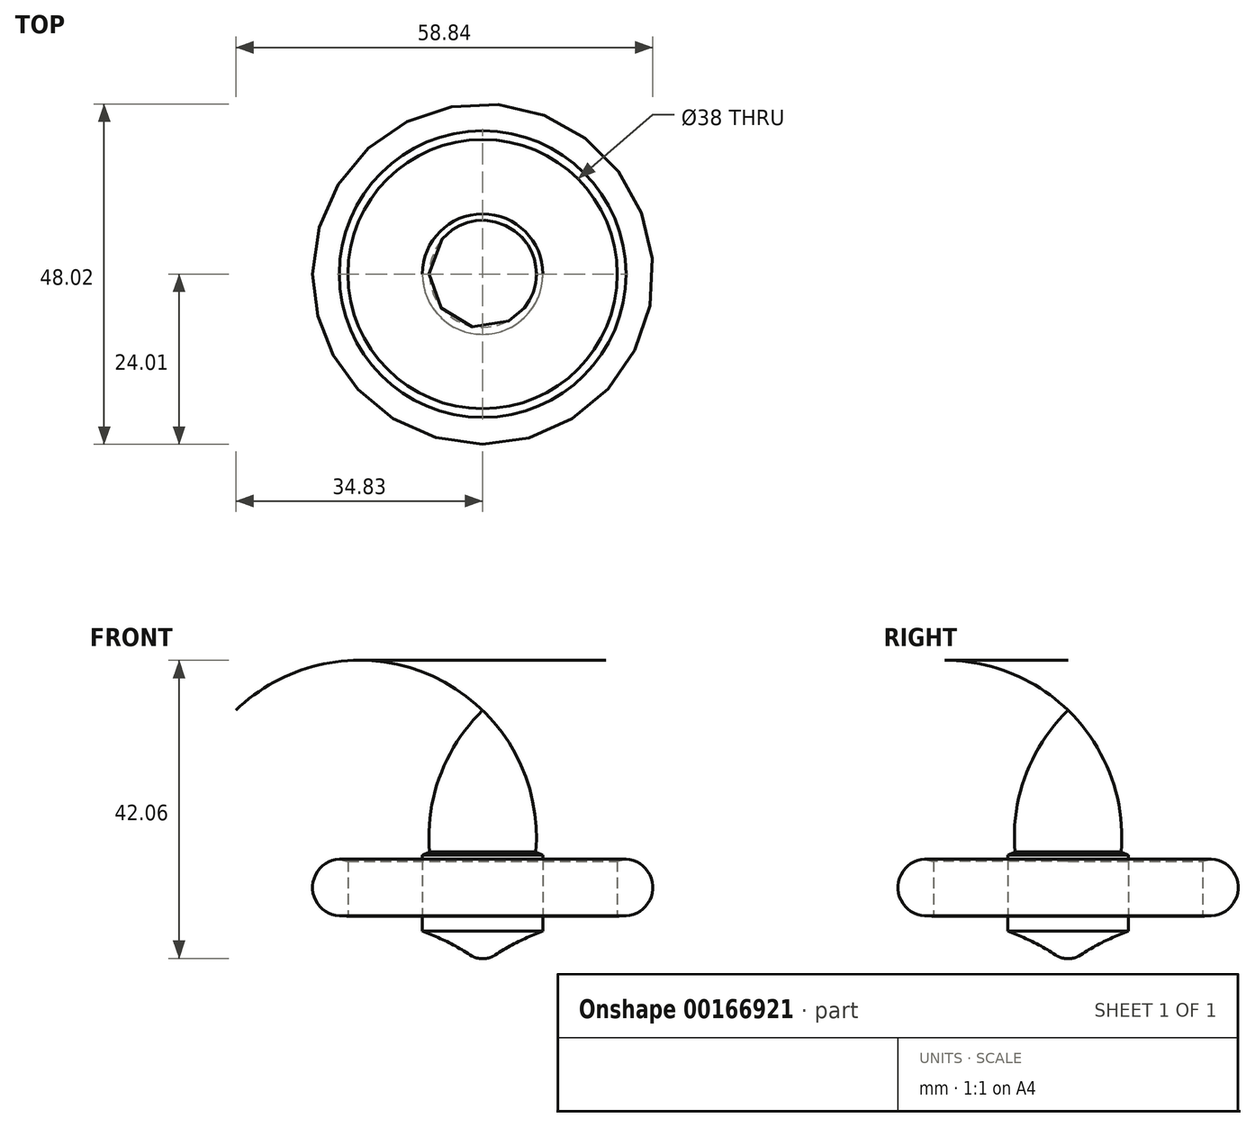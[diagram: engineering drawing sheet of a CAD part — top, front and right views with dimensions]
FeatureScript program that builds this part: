
annotation { "Feature Type Name" : "Feature", "Feature Type Description" : "" }
export const myFeature = defineFeature(function(context is Context, id is Id, definition is map)
    precondition{}
    {
        {
            var Q0;
            Q0=qCreatedBy(makeId("Front.planeOp"),FACE);
            var sketch = newSketch(context, id + "F0", { "sketchPlane" : qUnion([Q0])});
            skArc(sketch, "E0", {"start": v(0, 35) * mm, "mid": v(-6, 25.84) * mm, "end": v(-7.5, 15) * mm});
            skArc(sketch, "E1", {"start": v(-20.22, 14) * mm, "mid": v(-13.77, 13.37) * mm, "end": v(-7.5, 15) * mm});
            skArc(sketch, "E2", {"start": v(-20.22, 14) * mm, "mid": v(-24, 10) * mm, "end": v(-20.22, 6) * mm});
            skArc(sketch, "E3", {"start": v(-1, 0) * mm, "mid": v(-10.17, 4.41) * mm, "end": v(-20.22, 6) * mm});
            skLineSegment(sketch, "E4", {"start": v(0, 35) * mm, "end": v(0, 0) * mm});
            skLineSegment(sketch, "E5", {"start": v(-1, 0) * mm, "end": v(0, 0) * mm});
            skSolve(sketch);
        }
        {
            var Q0;
            Q0=qCreatedBy(makeId("Front.planeOp"),FACE);
            var sketch = newSketch(context, id + "F1", { "sketchPlane" : qUnion([Q0])});
            skLineSegment(sketch, "E6", {"start": v(0, 0) * mm, "end": v(0, 42.09) * mm, "construction": true});
            skSolve(sketch);
        }
        {
            var Q0;
            Q0=makeQuery(id+"F0.imprint","IMPRINT",FACE,{"disambiguationData":[TD([[makeQuery(id+"F0.imprint","IMPRINT",EDGE,{"derivedFrom":sQuery(id+"F0.wireOp",EDGE,"E0")}),1.0]])]});
            var Q1;
            Q1=sQuery(id+"F1.wireOp",EDGE,"E6");
            revolve(context, id + "F2", {"entities" : qUnion([Q0]), "axis" : qUnion([Q1]), "revolveType" : RevolveType.FULL});
        }
        {
            var Q0;
            Q0=makeQuery(id+"F2.opRevolve","SWEPT_EDGE",EDGE,{"disambiguationData":[OSD([sQuery(id+"F0.wireOp",EDGE,"E3"),sQuery(id+"F0.wireOp",EDGE,"E5")])]});
            fillet(context, id + "F3", {"entities" : qUnion([Q0]), "radius" : 2 * mm, "tangentPropagation" : true, "allowEdgeOverflow" : false});
        }
        {
            var Q0;
            Q0=qCreatedBy(makeId("Top.planeOp"),FACE);
            var sketch = newSketch(context, id + "F4", { "sketchPlane" : qUnion([Q0])});
            skCircle(sketch, "E7", {"center": v(0, 0) * mm, "radius": 19 * mm});
            skCircle(sketch, "E8", {"center": v(0, 0) * mm, "radius": 8.5 * mm});
            skSolve(sketch);
        }
        {
            var Q0;
            Q0 = qSketchRegion(id + "F4", true);
            extrude(context, id + "F5", {"entities" : qUnion([Q0]), "operationType" : NewBodyOperationType.REMOVE, "depth" : 25 * mm});
        }
    });
